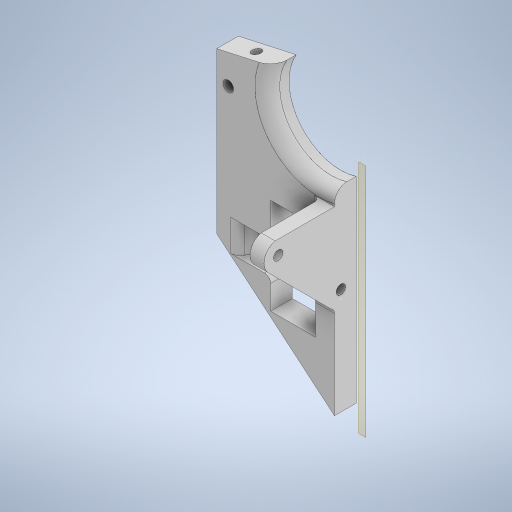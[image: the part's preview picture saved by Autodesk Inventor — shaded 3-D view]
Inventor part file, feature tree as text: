
AUTODESK INVENTOR PART (.ipt)
format: ipt  version: 2023 (Build 270158000, 158)  size: 458,240 bytes
history: native  units: in
note: dims shown in document units (in); Inventor stores cm internally (conversion verified against a paired STEP export)
features: sketch x27, other x6, extrude x1, projected_geometry x1
ambient origin geometry x8: Origin, YZ Plane, XZ Plane, XY Plane, X Axis, Y Axis, Z Axis, Center Point
bodies: Body1 (feature_tree)
feature tree (35):
  other  "sciana PRE 2.0.ipt"
  extrude  "Wyciągnięcie proste1"  Depth=0.3937in
  other  "Bryła1::sciana PRE 2.0.ipt"
  other  "Bryła wyprowadzona1"
  sketch  "Szkic1"
  sketch  "Szkic2"
  sketch  "Szkic3"
  sketch  "Szkic4"
  sketch  "Szkic5"
  sketch  "Szkic6"
  sketch  "Szkic7"
  sketch  "Szkic8"
  sketch  "Szkic9"
  sketch  "Szkic10"
  sketch  "Szkic11"
  sketch  "Szkic12"
  sketch  "Szkic13"
  sketch  "Szkic14"
  sketch  "Szkic15"
  sketch  "Szkic16"
  sketch  "Szkic17"
  sketch  "Szkic18"
  sketch  "Szkic19"
  sketch  "Szkic20"
  sketch  "Szkic21"
  sketch  "Szkic22"
  sketch  "Szkic23"
  sketch  "Szkic24"
  sketch  "Szkic25"
  sketch  "Szkic26"
  other  "Płaszczyzna konstrukcyjna1"
  other  "Płaszczyzna konstrukcyjna2"
  sketch  "Szkic27"
  projected_geometry  "Pętla rzutowana1"
  other  "Bryła1"
